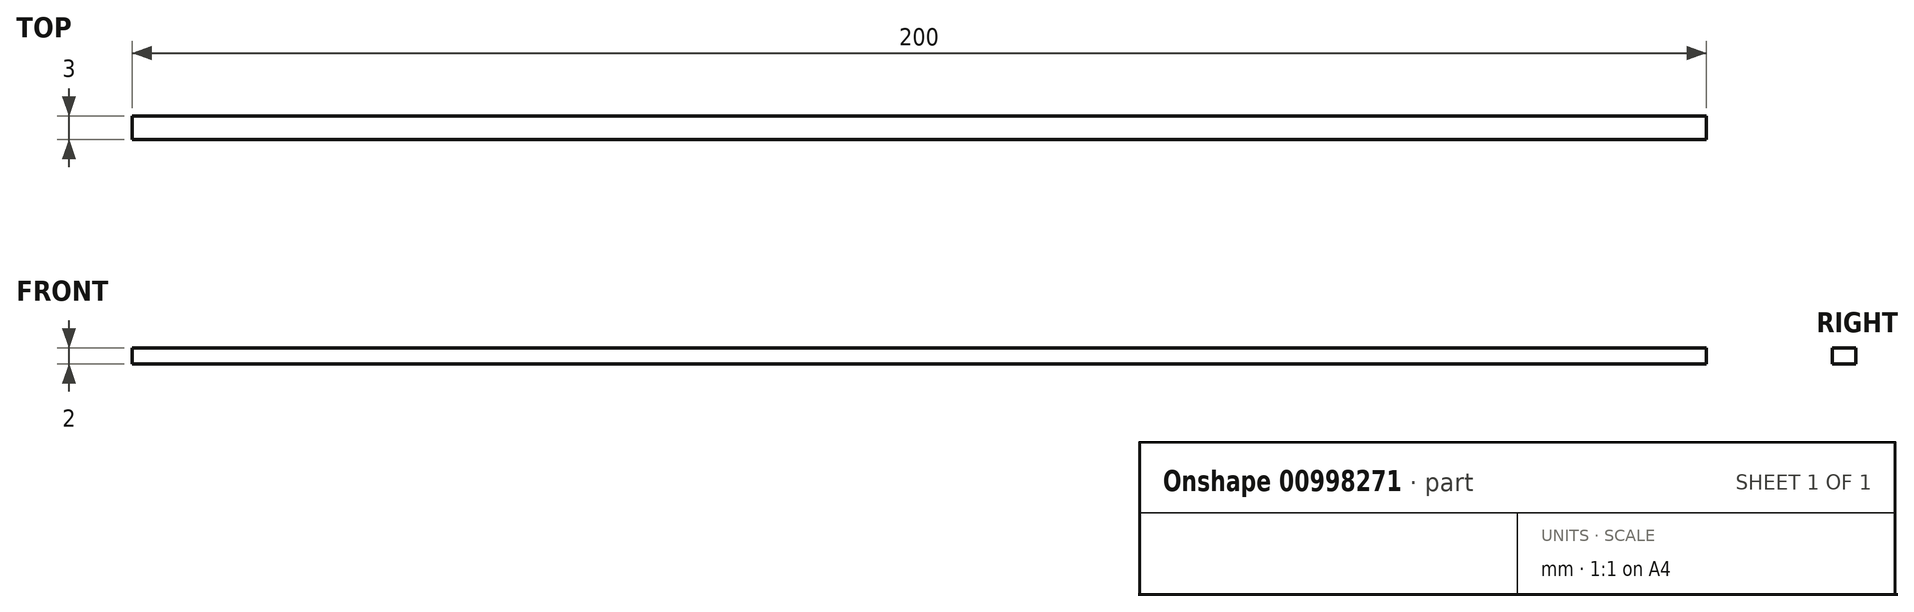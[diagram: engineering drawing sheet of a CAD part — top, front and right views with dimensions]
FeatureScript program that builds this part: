
annotation { "Feature Type Name" : "Feature", "Feature Type Description" : "" }
export const myFeature = defineFeature(function(context is Context, id is Id, definition is map)
    precondition{}
    {
        {
            var Q0;
            Q0=qCreatedBy(makeId("Top.planeOp"),FACE);
            var sketch = newSketch(context, id + "F0", { "sketchPlane" : qUnion([Q0])});
            skLineSegment(sketch, "E0.bottom", {"start": v(-97.03, -6.92) * mm, "end": v(102.97, -6.92) * mm});
            skLineSegment(sketch, "E0.top", {"start": v(-97.03, -9.92) * mm, "end": v(102.97, -9.92) * mm});
            skLineSegment(sketch, "E0.left", {"start": v(-97.03, -6.92) * mm, "end": v(-97.03, -9.92) * mm});
            skLineSegment(sketch, "E0.right", {"start": v(102.97, -6.92) * mm, "end": v(102.97, -9.92) * mm});
            skSolve(sketch);
        }
        {
            var Q0;
            Q0 = qSketchRegion(id + "F0", true);
            extrude(context, id + "F1", {"entities" : qUnion([Q0]), "depth" : 2 * mm, "offsetDistance" : 25.4 * mm});
        }
    });
